# Revit family: Faucet-Two-Handle-American_Standard-Town_Square_S-7455801_Series.rfaxxxx
name_source: partatom
category: Plumbing Fixtures
units: mm (PartAtom-declared; Revit-internal decimal feet)

## family parameters
Always vertical = No
Cut with Voids When Loaded = No
OmniClass Number = 23.45.55.17
OmniClass Title = Mixing Faucets
Part Type = Normal
Room Calculation Point = No
Round Connector Dimension = Use Diameter
Shared = Yes
Work Plane-Based = Yes

## types (4) — shared parameters
ADA Compliant = Yes
Assembly Code = D2020300
CEC Compliant = Yes
CW Connection = Yes
CWFU = 1.5
CalGreen Compliant = Yes
Cold Water Connection Diameter = 3/8"
Compliance Certifications = ANSI A117.1, ASME A112.18.1, CSA B125.1, NSF 61/Section 9, NSF 372, CALGreen, CEC Certified and EPA WaterSense
Default Elevation = 0"
Description = Town Square® S 8-Inch Widespread 2-Handle Bathroom Faucet 1.2 gpm/4.5 L/min With Lever Handles
Flow Rate = 1.2 gpm/ 4.5 L/min.
HW Connection = Yes
HWFU = 1.5
Height = 4 1/16"
Hot Water Connection Diameter = 0"
Installation Type = Deck Mounted
Length = 5 3/16"
Manufacturer = American Standard
Pop-up Drain Depth = 4"
Pop-up Drain Width from Faucet Centre = 5"
Price = Prices may vary. Please consult Manufacturer Representative for most up-to-date price list.
Product Documentation Link = https://americanstandard.box.com
Product Page URL = https://www.americanstandard-us.com
Revised Date = 07/25/2022
URL = https://www.americanstandard-us.com
Vent Connection = No
WFU = 2
Warranty Information = Limited Lifetime Function and Finish Warranty
Waste Connection = No
Width = 13 7/16"

## per-type parameters (varying)
| type | Finish | Material |
| 7455.801.002 | Cast Brass-American Standard-002-Polished Chrome | Cast Brass-American Standard-002-Polished Chrome |
| 7455.801.013 | Cast Brass-American Standard-013-Polished Nickel PVD | Cast Brass-American Standard-013-Polished Nickel PVD |
| 7455.801.295 | Cast Brass-American Standard-295-Brushed Nickel | Cast Brass-American Standard-295-Brushed Nickel |
| 7455.801.278 | Cast Brass-American Standard-278-Legacy Bronze | Cast Brass-American Standard-278-Legacy Bronze |

note: column(s) folded — value = type name in every type: Model

## geometry (parser evidence)
native form markers: Sweep x2
no freeform markers — native parametric forms only
